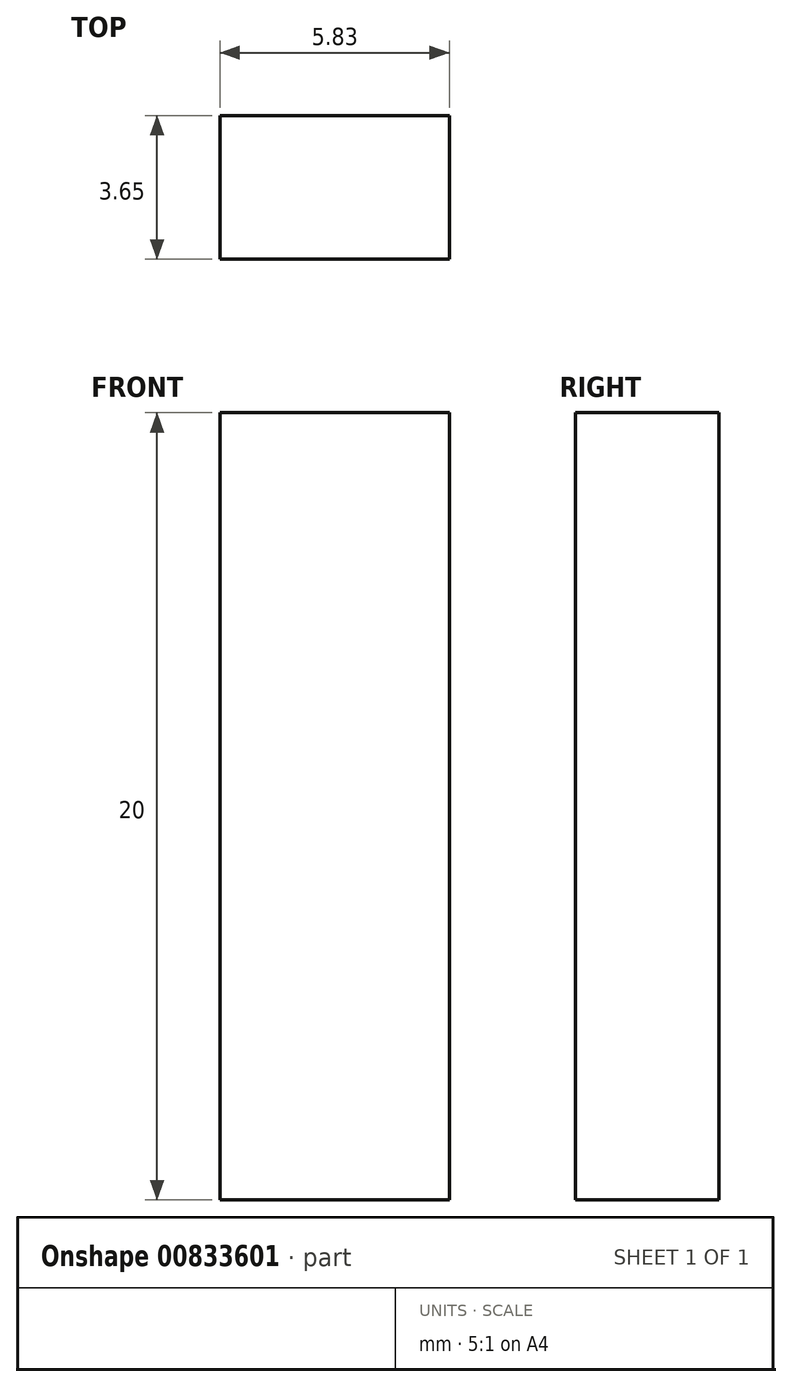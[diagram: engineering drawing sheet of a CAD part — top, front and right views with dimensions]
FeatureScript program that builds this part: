
annotation { "Feature Type Name" : "Feature", "Feature Type Description" : "" }
export const myFeature = defineFeature(function(context is Context, id is Id, definition is map)
    precondition{}
    {
        {
            var Q0;
            Q0=qCreatedBy(makeId("Top.planeOp"),FACE);
            var sketch = newSketch(context, id + "F0", { "sketchPlane" : qUnion([Q0])});
            skLineSegment(sketch, "E0", {"start": v(-3875, -1830.73) * mm, "end": v(-3869.17, -1830.73) * mm});
            skLineSegment(sketch, "E1", {"start": v(-3869.17, -1830.73) * mm, "end": v(-3869.17, -1834.38) * mm});
            skLineSegment(sketch, "E2", {"start": v(-3869.17, -1834.38) * mm, "end": v(-3875, -1834.38) * mm});
            skLineSegment(sketch, "E3", {"start": v(-3875, -1834.38) * mm, "end": v(-3875, -1830.73) * mm});
            skSolve(sketch);
        }
        {
            var Q0;
            Q0=makeQuery(id+"F0.imprint","IMPRINT",FACE,{"disambiguationData":[TD([[makeQuery(id+"F0.imprint","IMPRINT",EDGE,{"derivedFrom":sQuery(id+"F0.wireOp",EDGE,"E0")}),-1.0]])]});
            extrude(context, id + "F1", {"entities" : qUnion([Q0]), "depth" : 20 * mm, "offsetDistance" : 25 * mm});
        }
    });
